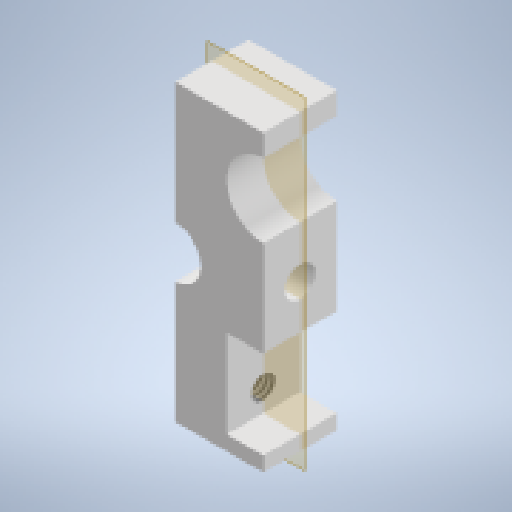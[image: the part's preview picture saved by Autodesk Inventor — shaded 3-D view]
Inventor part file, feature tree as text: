
AUTODESK INVENTOR PART (.ipt)
format: ipt  version: 2023 (Build 270158000, 158)  size: 235,008 bytes
history: native  units: mm
features: extrude x7, sketch x7, thread x2, plane x1
ambient origin geometry x8: Origin, YZ Plane, XZ Plane, XY Plane, X Axis, Y Axis, Z Axis, Center Point
bodies: Solid1 (feature_tree)
feature tree (17):
  extrude  "Extrusion1"  Depth=20.0mm
  plane  "Work Plane1"
  extrude  "Extrusion2"  Depth=2.0mm
  extrude  "Extrusion3"  Depth=4.0mm
  extrude  "Extrusion4"  Depth=5.0mm TaperAngle=0.0deg
  thread  "Thread1"  [1 undecoded]
  thread  "Thread2"  [1 undecoded]
  extrude  "Extrusion5"  Depth=8.0mm TaperAngle=0.0deg
  extrude  "Extrusion6"  Depth=1.6mm
  extrude  "Extrusion7"  Depth=10.0mm
  sketch  "Sketch1"  dims[d0=20.0mm d1=20.0mm]
  sketch  "Sketch2"  dims[d2=4.0mm d6=2.0mm]
  sketch  "Sketch3"  dims[d7=2.0mm d8=4.0mm]
  sketch  "Sketch4"  dims[d9=2.0mm d10=5.0mm d11=0.0mm d12=5.0mm d13=1.8mm d14=0.0mm]
  sketch  "Sketch5"  dims[d15=3.5mm d16=8.0mm d17=0.0mm]
  sketch  "Sketch6"  dims[d18=1.6mm d19=1.6mm]
  sketch  "Sketch7"  dims[d20=2.5mm d21=2.5mm d22=2.5mm d23=2.5mm d24=5.0mm d25=0.0mm d26=5.0mm d27=0.0mm d28=5.0mm d29=0.0mm d30=5.0mm d31=0.0mm d32=2.5mm d33=1.0mm d34=6.0mm d35=5.0mm d36=4.0mm d37=5.0mm d38=0.0mm d39=2.5mm d40=10.0mm d41=2.05mm d42=12.0mm d43=0.0mm d44=6.0mm]
note: 2 required parameter values undecoded (feature->parameter linkage not recoverable at this tier; creation-order binding heuristic only, values carry confidence <= 0.55)
